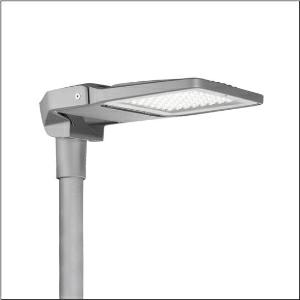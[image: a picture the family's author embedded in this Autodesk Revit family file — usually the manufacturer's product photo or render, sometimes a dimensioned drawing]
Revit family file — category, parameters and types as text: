
# Revit family: floodlight_fl_20_mini___pl43_5xa7672b1a4ac_75ab
name_source: partatom
category: Lighting Fixtures
units: mm (PartAtom-declared; Revit-internal decimal feet)

## family parameters
Cut with Voids When Loaded = No
Host = Face
Light Source = No
Part Type = Normal
Room Calculation Point = No
Round Connector Dimension = Use Diameter
Shared = No

## types (1)
- --- (1 x LED 3000K / CRI = 80 (unbekannt), 5220 lm, 3000K)
    Apparent Load = 51 VA
    CIE Flux Codes = 32 74 99 100 100
    Color Rendering = 80
    Color Temperature = 3000K
    Default Elevation = 1800 mm
    Description = Floodlight FL 20 mini, floodlight, primary light control with lens, of plastic, primary optical cover: protective disc, of toughened safety glass, transparent, light distribution: PL43, light emission: direct distribution, primary light characteristic: asymmetric, installation type: surface-mounted, LED, High Power LED, rated luminous flux: 5.220lm, luminous efficacy: 102lm/W, light colour: 830, colour temperature: 3000K, control gear: ECG Plus, control: flexible luminous flux parameterisation, time-dependent luminous flux control, digital communication interface, overheat protection, power reduction, electronic power reduction, with terminal, 5-pole, max. 2.5mm², mains connection: 220..240V, AC, 50/60Hz, rated input power: 51W, LED unit, of diecast aluminium, powder-coated, Siteco® metallic grey (DB 702S), corrosivity category C5 mid according to DIN EN ISO 12944, incl. 1x M20 cable gland for cable Ø 6.5..12mm, inclination adjustable: 0°, 5°, 10°, 15°, please order mast flange separately, length: 565mm, width: 335mm, height: 119mm, housing frame, of diecast aluminium, powder-coated, Siteco® metallic grey (DB 702S), mast flange adapter, of steel, powder-coated, Siteco® metallic grey (DB 702S), DALI, protection rating (complete): IP66, insulation class (complete): insulation class II (safety insulation), certification: CE, ENEC, VDE, protection symbol: D, permissible operating ambient temperature: -40..+40°C, permissible operating ambient temperature for outdoor applications: -40..+50°C, standard: DIN EN 12944, packaging unit: 1 piece

Light Distribution: PL43
    Height = 62 mm  [stored 0.203412 ft]
    Lamp = 1 x LED 3000K / CRI >= 80 (unbekannt)
    Lamp Light Flux = 5220 lm
    Lamp count = 1
    Length = 565 mm
    Luminous efficacy = 102 lm/W
    Manufacturer = Siteco
    ModVariant = No
    Model = 5XA7672B1A4AC
    Mounting Place = Wall
    Mounting Type = Surface mounted
    Number of Poles = 1
    OnlyDefault = Yes
    Power Factor = 1
    Product Name = Floodlight FL 20 mini | PL43
    Product group = floodlight | wall mounted
    ProductGroupID = 2001
    Protection Class = Protection class II
    Protection Degree = IP 66
    RLX_Detail_Level = 1
    RLX_Emergency_Light_Flux = 0 lm
    RLX_Emergency_Type = 0
    RLX_Emergency_Type_DB = No
    RlxData = <blob elided: 101865 chars, md5=870cf848>
    Socket = socket
    Standby Power = 0 W
    System Light Flux = 5220 lm
    System Power = 51 W
    Type Comments = factory setting: luminous flux: 100 % | dim-lin: 254 | 520 mA
    Type Image = l_1005946.jpg
    URL = http://relux.com
    VarID = @adj_164141
    Voltage = 0 V
    Weight = 0.00 kg
    Width = 335 mm

note: [stored X ft] marks values corroborated as IEEE doubles in the binary element streams (Revit-internal decimal feet)

## geometry (parser evidence)
native form markers: Blend x4, Sweep x11
no freeform markers — native parametric forms only
